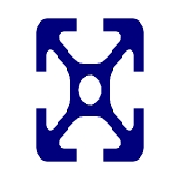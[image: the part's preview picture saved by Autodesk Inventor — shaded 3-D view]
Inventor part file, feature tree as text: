
AUTODESK INVENTOR PART (.ipt)
format: ipt  version: 2020 (Build 240168000, 168)  size: 271,872 bytes
history: native  units: mm
features: other x16, sketch x8, plane x1, split x1
ambient origin geometry x8: Origin, YZ Plane, XZ Plane, XY Plane, X Axis, Y Axis, Z Axis, Center Point
bodies: Body (feature_tree)
feature tree (26):
  other  "Řízená délka"
  other  "Těleso1"
  other  "Start Plane"
  other  "End Plane"
  other  "iFeatureSketch"
  other  "DRAZKA_20:1"
  other  "DRAZKA_20:2"
  other  "DRAZKA_20:3"
  other  "DRAZKA_20:4"
  other  "DIRA_20:1"
  other  "DRAZKA_20:1Axis"
  other  "DRAZKA_20:2Axis"
  other  "DRAZKA_20:3Axis"
  other  "DRAZKA_20:4Axis"
  other  "DIRA_20:1Axis"
  plane  "Work Plane5"
  split  "Split1"
  sketch  "Sketch"  dims[d2=20.0mm d3=20.0mm d4=2.0mm d9=10.0mm d10=100.0mm d11=0.13mm d12=0.0mm d15=0.83mm d16=0.83mm d17=9.8mm d18=3.0mm d19=4.55mm d20=45.0deg d21=5.2mm d22=1.8mm d24=1.0mm d26=0.83mm d27=0.83mm d28=9.8mm d29=3.0mm d30=4.55mm d31=45.0deg d32=5.2mm d33=1.8mm d35=1.0mm d37=0.83mm d38=0.83mm d39=9.8mm d40=3.0mm d41=4.55mm d42=45.0deg d43=5.2mm d44=1.8mm d46=1.0mm d48=0.83mm d49=0.83mm d50=9.8mm d51=3.0mm d52=4.55mm d53=45.0deg d54=5.2mm d55=1.8mm d57=1.0mm d59=4.3mm d60=0.0mm d61=0.0mm d62=0.0mm d63=0.0mm d64=0.0mm d65=0.0mm d66=0.0mm d67=0.0mm d76=90.0deg d14=90.0mm]
  sketch  "Náčrt11"
  other  "Pracovní rovina4"
  sketch  "Náčrt12"
  sketch  "Náčrt6"
  sketch  "Náčrt7"
  sketch  "Náčrt8"
  sketch  "Náčrt9"
  sketch  "Náčrt10"
